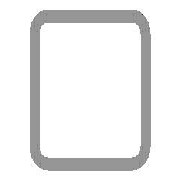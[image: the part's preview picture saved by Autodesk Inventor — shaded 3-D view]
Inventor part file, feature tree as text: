
AUTODESK INVENTOR PART (.ipt)
format: ipt  version: 2025 (Build 290162010, 162A)  size: 133,632 bytes
history: native  units: mm (DEFAULTED — no unit token found)
features: other x4, sketch x1, plane x1
ambient origin geometry x8: Origin, YZ Plane, XZ Plane, XY Plane, X Axis, Y Axis, Z Axis, Center Point
bodies: Solid1 (feature_tree), Body (feature_tree)
feature tree (6):
  parser-record x1  (decoder bookkeeping rows leaked as tree rows — omitted from the tree; the rows remain in map.json)
  other  "Driven Length"
  other  "Start Plane"
  other  "End Plane"
  sketch  "Sketch3"  dims[d3=2870.0mm d4=0.0mm d7=6.0mm d9=80.0mm d11=80.0mm d12=3.0mm d13=-0.0mm d14=2870.0mm d15=40.0mm d16=40.0mm d17=90.0deg d18=2870.0mm]
  plane  "Work Plane3"
